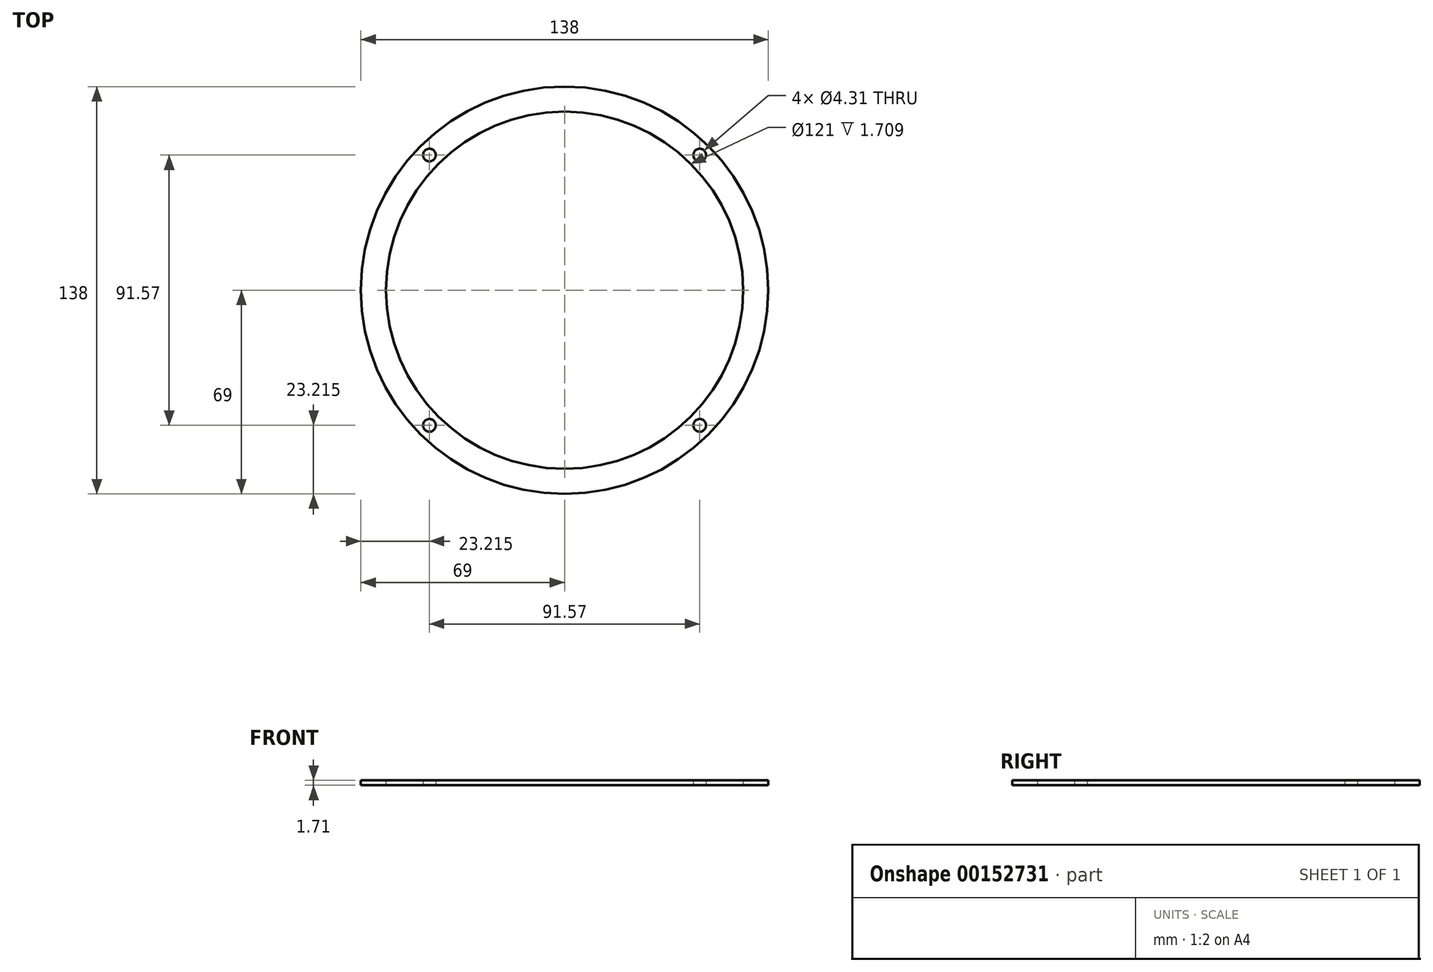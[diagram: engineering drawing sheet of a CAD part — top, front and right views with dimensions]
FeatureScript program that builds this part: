
annotation { "Feature Type Name" : "Feature", "Feature Type Description" : "" }
export const myFeature = defineFeature(function(context is Context, id is Id, definition is map)
    precondition{}
    {
        {
            var Q0;
            Q0=qCreatedBy(makeId("Top.planeOp"),FACE);
            var sketch = newSketch(context, id + "F0", { "sketchPlane" : qUnion([Q0])});
            skCircle(sketch, "E0", {"center": v(0, 0) * mm, "radius": 60.5 * mm});
            skCircle(sketch, "E1", {"center": v(0, 0) * mm, "radius": 69 * mm});
            skCircle(sketch, "E2", {"center": v(-45.79, 45.79) * mm, "radius": 4.25 * mm, "construction": true});
            skLineSegment(sketch, "E3.bottom", {"start": v(-45.79, 45.79) * mm, "end": v(45.79, 45.79) * mm, "construction": true});
            skLineSegment(sketch, "E3.top", {"start": v(-45.79, -45.79) * mm, "end": v(45.79, -45.79) * mm, "construction": true});
            skLineSegment(sketch, "E3.left", {"start": v(-45.79, 45.79) * mm, "end": v(-45.79, -45.79) * mm, "construction": true});
            skLineSegment(sketch, "E3.right", {"start": v(45.79, 45.79) * mm, "end": v(45.79, -45.79) * mm, "construction": true});
            skCircle(sketch, "E4", {"center": v(-45.79, 45.79) * mm, "radius": 2.15 * mm});
            skCircle(sketch, "E5", {"center": v(-45.79, -45.79) * mm, "radius": 2.15 * mm});
            skCircle(sketch, "E6", {"center": v(45.79, -45.79) * mm, "radius": 2.15 * mm});
            skCircle(sketch, "E7", {"center": v(45.79, 45.79) * mm, "radius": 2.15 * mm});
            skSolve(sketch);
        }
        {
            var Q0;
            Q0=qSketchRegion(id+"F0",true);
            extrude(context, id + "F1", {"entities" : qUnion([Q0]), "depth" : 1.7 * mm});
        }
    });
